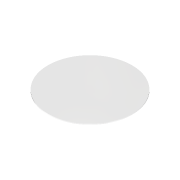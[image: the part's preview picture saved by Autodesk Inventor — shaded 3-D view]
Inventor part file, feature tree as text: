
AUTODESK INVENTOR PART (.ipt)
format: ipt  version: 2022 (Build 260153000, 153)  size: 78,848 bytes
history: native  units: mm
features: extrude x1, sketch x1
ambient origin geometry x8: Origin, YZ Plane, XZ Plane, XY Plane, X Axis, Y Axis, Z Axis, Center Point
bodies: Volumenkörper1 (feature_tree)
feature tree (2):
  extrude  "Extrusion1"  Depth=0.125mm TaperAngle=0.0deg
  sketch  "Skizze1"  dims[d0=12.0mm d1=0.125mm d2=0.0mm]
